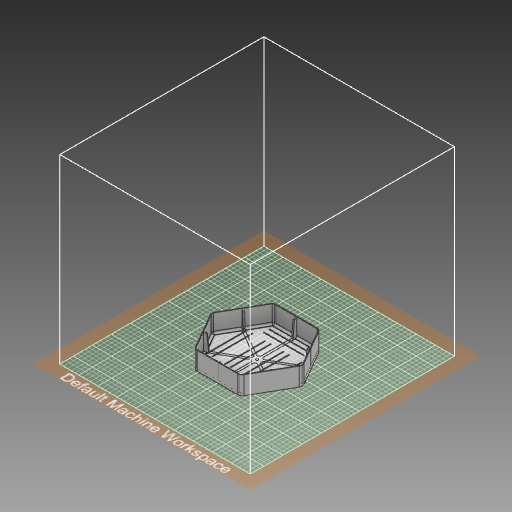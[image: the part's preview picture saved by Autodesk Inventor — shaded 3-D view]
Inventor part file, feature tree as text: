
AUTODESK INVENTOR PART (.ipt)
format: ipt  version: 2019 (Build 230136000, 136)  size: 856,576 bytes
history: native  units: mm
features: projected_geometry x23, sketch x9, extrude x5, plane x3, fillet x3, other x3, shell x1, pattern_circular x1
ambient origin geometry x8: Origin, YZ Plane, XZ Plane, XY Plane, X Axis, Y Axis, Z Axis, Center Point
bodies: Solid1 (feature_tree)
feature tree (48):
  extrude  "Extrusion1"  Depth=40.0mm TaperAngle=0.0deg
  shell  "Shell1"  Thickness=1.5mm
  extrude  "Extrusion9"  Depth=10.0mm
  plane  "Work Plane1"
  plane  "Work Plane2"
  plane  "Work Plane3"
  sketch  "Sketch12"  dims[d55=5.0mm]
  extrude  "Extrusion5"  Depth=5.0mm
  extrude  "Extrusion6"  TaperAngle=60.0deg  [1 undecoded]
  extrude  "Extrusion8"  TaperAngle=90.0deg  [1 undecoded]
  pattern_circular  "Circular Pattern1"  [2 undecoded]
  fillet  "Fillet1"  Radius=8.0mm
  fillet  "Fillet2"  Radius=36.0mm
  fillet  "Fillet4"  Radius=60.0mm
  sketch  "Sketch5"  dims[d12=1.0mm d37=5.0mm]
  sketch  "Sketch6"  dims[d44=10.0mm d45=60.0deg]
  sketch  "Sketch7"  dims[d46=90.0deg d47=90.0deg]
  other  "Work Axis4"
  other  "Work Axis5"
  other  "Work Axis6"
  sketch  "Sketch13"  dims[d56=2.0mm d57=3.0mm d58=8.0mm d59=36.0mm d60=0.0mm d70=60.0mm d72=360.0deg d74=60.0mm d75=360.0deg d77=3.0mm d78=30.0mm d79=20.0mm d80=0.0mm d138=11.0mm d139=87.0mm d140=40.0mm d142=40.5mm d143=10.0mm d145=10.0mm d147=130.0mm d149=0.5mm d150=0.0mm d151=1.0mm d152=1.0mm d153=1.0mm d154=1.0mm d155=1.0mm d156=1.0mm]
  sketch  "Sketch1"  dims[d0=88.0mm d2=40.0mm d3=0.0mm d4=1.5mm]
  sketch  "Sketch4"  dims[d10=4.0mm d11=10.0mm]
  projected_geometry  "Projected Loop3"
  sketch  "Sketch8"  dims[d52=5.5mm]
  projected_geometry  "Projected Loop4"
  sketch  "Sketch9"  dims[d53=0.01mm d54=0.0mm]
  projected_geometry  "Projected Loop5"
  projected_geometry  "Projected Loop6"
  projected_geometry  "Projected Loop7"
  projected_geometry  "Projected Loop8"
  projected_geometry  "Projected Loop9"
  projected_geometry  "Projected Loop10"
  projected_geometry  "Projected Loop11"
  projected_geometry  "Projected Loop12"
  projected_geometry  "Projected Loop13"
  projected_geometry  "Projected Loop14"
  projected_geometry  "Projected Loop15"
  projected_geometry  "Projected Loop16"
  projected_geometry  "Projected Loop17"
  projected_geometry  "Projected Loop18"
  projected_geometry  "Projected Loop19"
  projected_geometry  "Projected Loop20"
  projected_geometry  "Projected Loop21"
  projected_geometry  "Projected Loop22"
  projected_geometry  "Projected Loop23"
  projected_geometry  "Projected Loop24"
  projected_geometry  "Projected Loop25"
note: 4 required parameter values undecoded (feature->parameter linkage not recoverable at this tier; creation-order binding heuristic only, values carry confidence <= 0.55)
